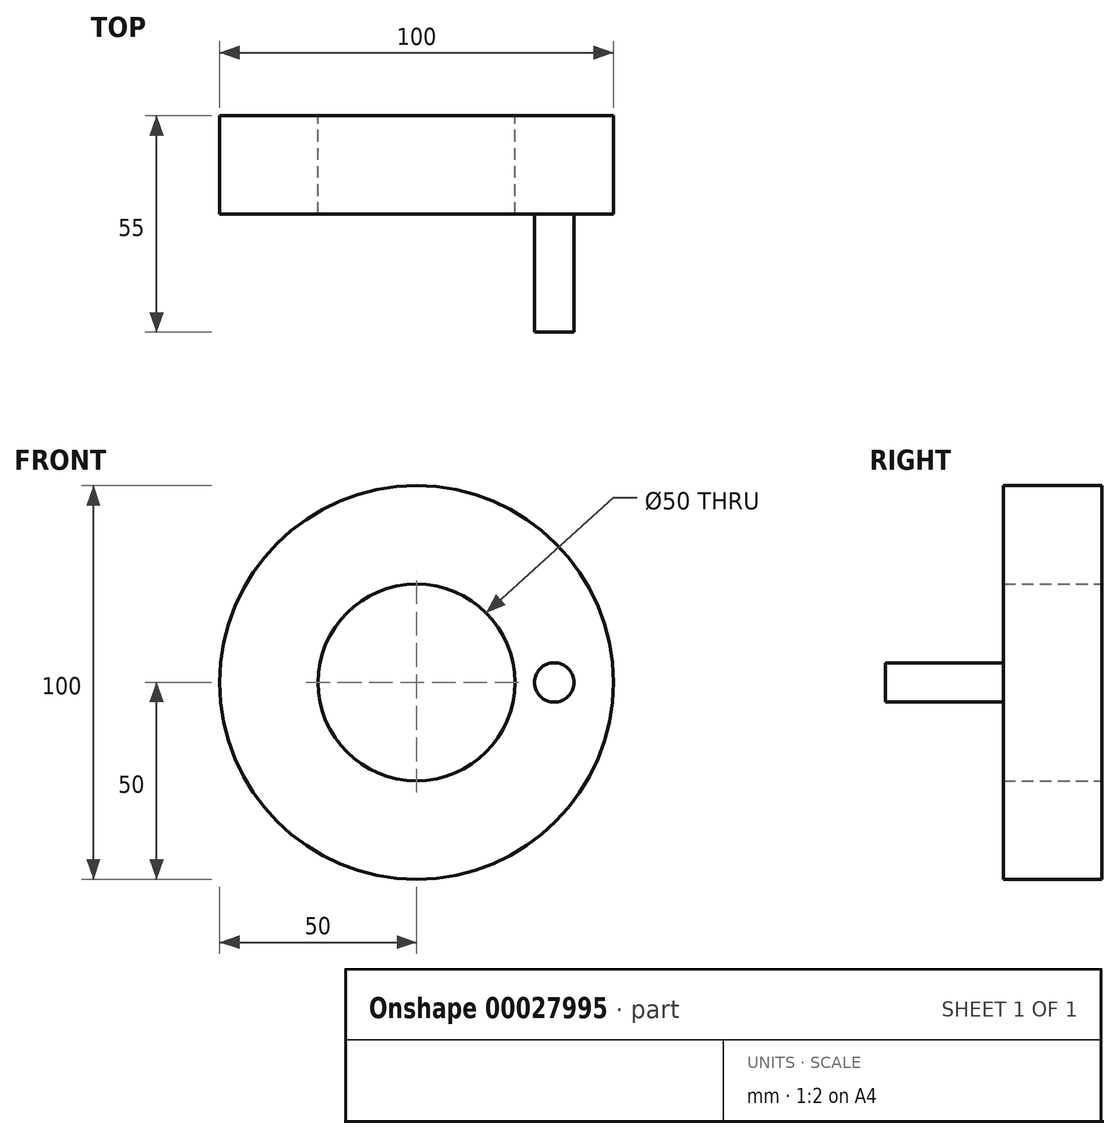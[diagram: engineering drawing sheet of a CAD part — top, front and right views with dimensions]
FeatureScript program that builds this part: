
annotation { "Feature Type Name" : "Feature", "Feature Type Description" : "" }
export const myFeature = defineFeature(function(context is Context, id is Id, definition is map)
    precondition{}
    {
        {
            var Q0;
            Q0=qCreatedBy(makeId("Front.planeOp"),FACE);
            var sketch = newSketch(context, id + "F0", { "sketchPlane" : qUnion([Q0])});
            skCircle(sketch, "E0", {"center": v(0, 0) * mm, "radius": 50 * mm});
            skCircle(sketch, "E1", {"center": v(0, 0) * mm, "radius": 25 * mm});
            skSolve(sketch);
        }
        {
            var Q0;
            Q0 = qSketchRegion(id + "F0", true);
            var Q1;
            Q1=makeQuery(id+"F0.imprint","IMPRINT",FACE,{"disambiguationData":[TD([[makeQuery(id+"F0.imprint","IMPRINT",EDGE,{"derivedFrom":sQuery(id+"F0.wireOp",EDGE,"E0")}),1.0]])]});
            extrude(context, id + "F1", {"entities" : qUnion([Q0, Q1]), "depth" : 25 * mm});
        }
        {
            var Q0;
            Q0=makeQuery(id+"F1.opExtrude","CAP_FACE",FACE,{"disambiguationData":[OSD([sQuery(id+"F0.wireOp",EDGE,"E0"),sQuery(id+"F0.wireOp",EDGE,"E1")])],"isStart":false});
            var sketch = newSketch(context, id + "F2", { "sketchPlane" : qUnion([Q0])});
            skCircle(sketch, "E2", {"center": v(35, 0) * mm, "radius": 5 * mm});
            skSolve(sketch);
        }
        {
            var Q0;
            Q0=makeQuery(id+"F2.imprint","IMPRINT",FACE,{"disambiguationData":[TD([[makeQuery(id+"F2.imprint","IMPRINT",EDGE,{"derivedFrom":sQuery(id+"F2.wireOp",EDGE,"E2")}),1.0]])]});
            extrude(context, id + "F3", {"entities" : qUnion([Q0]), "operationType" : NewBodyOperationType.ADD, "depth" : 30 * mm});
        }
    });
